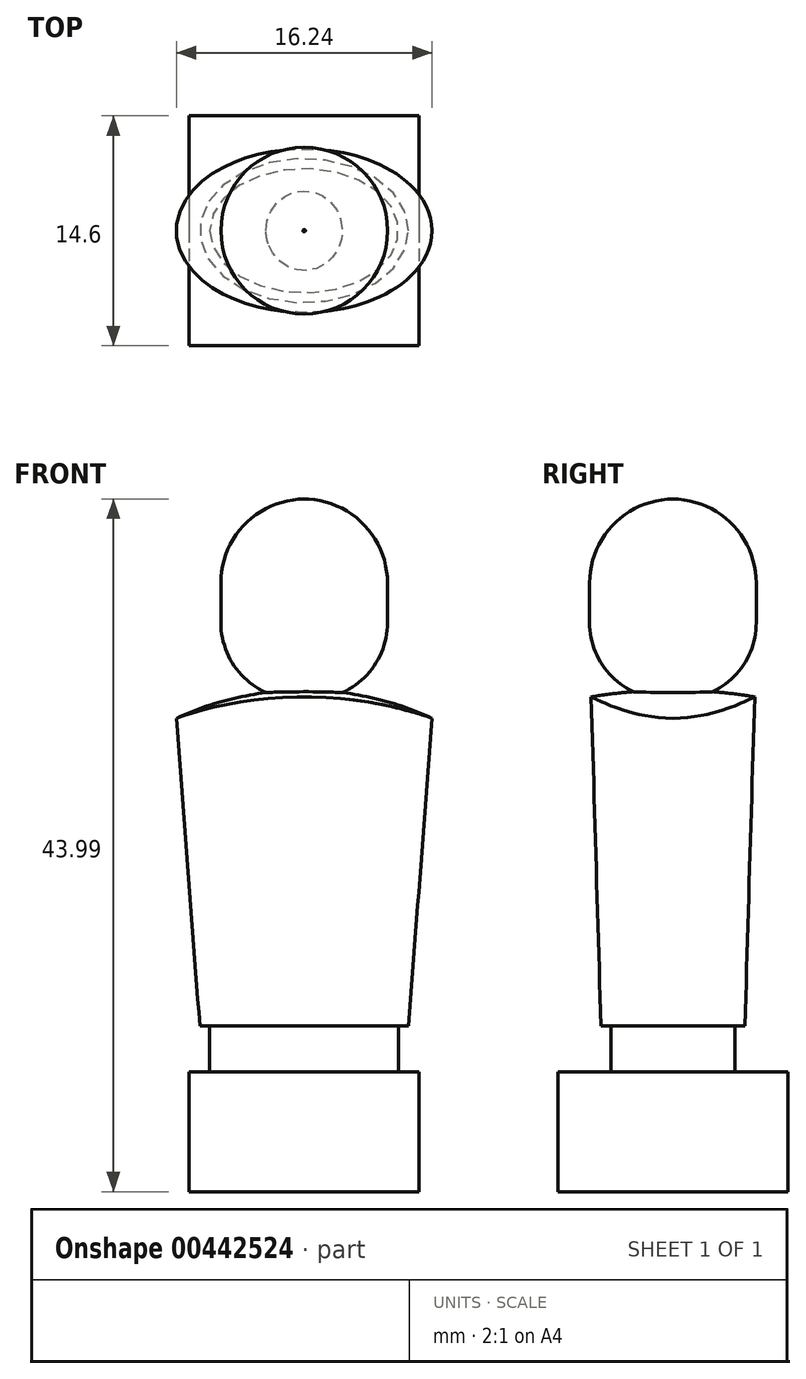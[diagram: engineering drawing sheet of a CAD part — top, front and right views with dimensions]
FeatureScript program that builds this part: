
annotation { "Feature Type Name" : "Feature", "Feature Type Description" : "" }
export const myFeature = defineFeature(function(context is Context, id is Id, definition is map)
    precondition{}
    {
        {
            var Q0;
            Q0=qCreatedBy(makeId("Top.planeOp"),FACE);
            var sketch = newSketch(context, id + "F0", { "sketchPlane" : qUnion([Q0])});
            skLineSegment(sketch, "E0.bottom", {"start": v(7.3, 7.3) * mm, "end": v(-7.3, 7.3) * mm});
            skLineSegment(sketch, "E0.top", {"start": v(7.3, -7.3) * mm, "end": v(-7.3, -7.3) * mm});
            skLineSegment(sketch, "E0.left", {"start": v(7.3, 7.3) * mm, "end": v(7.3, -7.3) * mm});
            skLineSegment(sketch, "E0.right", {"start": v(-7.3, 7.3) * mm, "end": v(-7.3, -7.3) * mm});
            skPoint(sketch, "E0.middle", {"position": v(0, 0) * mm});
            skSolve(sketch);
        }
        {
            var Q0;
            Q0=makeQuery(id+"F0.imprint","IMPRINT",FACE,{"disambiguationData":[TD([[makeQuery(id+"F0.imprint","IMPRINT",EDGE,{"derivedFrom":sQuery(id+"F0.wireOp",EDGE,"E0.bottom")}),1.0]])]});
            extrude(context, id + "F1", {"entities" : qUnion([Q0]), "depth" : 7.62 * mm});
        }
        {
            var Q0;
            Q0=makeQuery(id+"F1.opExtrude","CAP_FACE",FACE,{"disambiguationData":[OSD([sQuery(id+"F0.wireOp",EDGE,"E0.bottom"),sQuery(id+"F0.wireOp",EDGE,"E0.top"),sQuery(id+"F0.wireOp",EDGE,"E0.left"),sQuery(id+"F0.wireOp",EDGE,"E0.right")])],"isStart":false});
            var sketch = newSketch(context, id + "F2", { "sketchPlane" : qUnion([Q0])});
            skEllipse(sketch, "E1", {"center": v(0, 0) * mm, "majorRadius": 6 * mm, "minorRadius": 3.94 * mm, "majorAxis": v(-1, 0)});
            skSolve(sketch);
        }
        {
            var Q0;
            Q0=makeQuery(id+"F2.imprint","IMPRINT",FACE,{"disambiguationData":[TD([[makeQuery(id+"F2.imprint","IMPRINT",EDGE,{"derivedFrom":sQuery(id+"F2.wireOp",EDGE,"E1")}),1.0]])]});
            extrude(context, id + "F3", {"entities" : qUnion([Q0]), "operationType" : NewBodyOperationType.ADD, "depth" : 2.92 * mm});
        }
        {
            var Q0;
            Q0=makeQuery(id+"F3.opExtrude","CAP_FACE",FACE,{"disambiguationData":[OSD([sQuery(id+"F2.wireOp",EDGE,"E1")])],"isStart":false});
            cPlane(context, id + "F4", {"entities" : qUnion([Q0]), "cplaneType" : CPlaneType.OFFSET, "offset" : 21.34 * mm, "width" : 152.4 * mm, "height" : 152.4 * mm});
        }
        {
            var Q0;
            Q0=makeQuery(id+"F3.opExtrude","CAP_FACE",FACE,{"disambiguationData":[OSD([sQuery(id+"F2.wireOp",EDGE,"E1")])],"isStart":false});
            var sketch = newSketch(context, id + "F5", { "sketchPlane" : qUnion([Q0])});
            skEllipse(sketch, "E2", {"center": v(0, 0) * mm, "majorRadius": 6.63 * mm, "minorRadius": 4.57 * mm, "majorAxis": v(1, 0)});
            skSolve(sketch);
        }
        {
            var Q0;
            Q0=qCreatedBy(id+"F4.planeOp",FACE);
            var sketch = newSketch(context, id + "F6", { "sketchPlane" : qUnion([Q0])});
            skEllipse(sketch, "E3", {"center": v(0, 0) * mm, "majorRadius": 8.26 * mm, "minorRadius": 5.2 * mm, "majorAxis": v(1, 0)});
            skSolve(sketch);
        }
        {
            var Q0;
            Q0 = qSketchRegion(id + "F5", true);
            var Q1;
            Q1 = qSketchRegion(id + "F6", true);
            loft(context, id + "F7", {"sheetProfilesArray" : [{ "sheetProfileEntities" : qUnion([Q0]) }, { "sheetProfileEntities" : qUnion([Q1]) }]});
        }
        {
            var Q0;
            Q0=qCreatedBy(makeId("Front.planeOp"),FACE);
            var sketch = newSketch(context, id + "F8", { "sketchPlane" : qUnion([Q0])});
            skPoint(sketch, "E4", {"position": v(0, 31.86) * mm});
            skArc(sketch, "E5", {"start": v(15.24, 24.42) * mm, "mid": v(0, 31.86) * mm, "end": v(-15.24, 24.42) * mm});
            skLineSegment(sketch, "E6", {"start": v(15.24, 24.42) * mm, "end": v(7.3, 0) * mm});
            skLineSegment(sketch, "E7", {"start": v(7.3, 0) * mm, "end": v(-7.3, 0) * mm});
            skLineSegment(sketch, "E8", {"start": v(-7.3, 0) * mm, "end": v(-15.24, 24.42) * mm});
            skSolve(sketch);
        }
        {
            var Q0;
            Q0=makeQuery(id+"F8.imprint","IMPRINT",FACE,{"disambiguationData":[TD([[makeQuery(id+"F8.imprint","IMPRINT",EDGE,{"derivedFrom":sQuery(id+"F8.wireOp",EDGE,"E5")}),1.0]])]});
            var Q1;
            Q1=sQuery(id+"F8.wireOp",EDGE,"E7");
            revolve(context, id + "F9", {"operationType" : NewBodyOperationType.INTERSECT, "entities" : qUnion([Q0]), "axis" : qUnion([Q1]), "revolveType" : RevolveType.FULL});
        }
        {
            var Q0;
            Q0=qCreatedBy(makeId("Front.planeOp"),FACE);
            var sketch = newSketch(context, id + "F10", { "sketchPlane" : qUnion([Q0])});
            skLineSegment(sketch, "E9", {"start": v(0, 31.3) * mm, "end": v(0, 44) * mm});
            skLineSegment(sketch, "E10", {"start": v(-5.3, 38.66) * mm, "end": v(-5.3, 36.14) * mm});
            skArc(sketch, "E11", {"start": v(0, 44) * mm, "mid": v(-3.74, 42.42) * mm, "end": v(-5.3, 38.66) * mm});
            skArc(sketch, "E12", {"start": v(-5.3, 36.14) * mm, "mid": v(-3.71, 32.55) * mm, "end": v(0, 31.3) * mm});
            skSolve(sketch);
        }
        {
            var Q0;
            Q0=makeQuery(id+"F10.imprint","IMPRINT",FACE,{"disambiguationData":[TD([[makeQuery(id+"F10.imprint","IMPRINT",EDGE,{"derivedFrom":sQuery(id+"F10.wireOp",EDGE,"E9")}),1.0]])]});
            var Q1;
            Q1=sQuery(id+"F10.wireOp",EDGE,"E9");
            revolve(context, id + "F11", {"operationType" : NewBodyOperationType.ADD, "entities" : qUnion([Q0]), "axis" : qUnion([Q1]), "revolveType" : RevolveType.FULL});
        }
    });
